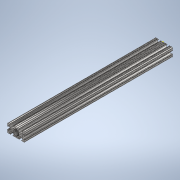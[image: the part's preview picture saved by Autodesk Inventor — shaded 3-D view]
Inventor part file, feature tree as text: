
AUTODESK INVENTOR PART (.ipt)
format: ipt  version: 2020 (Build 240168000, 168)  size: 347,648 bytes
history: native  units: in
note: dims shown in document units (in); Inventor stores cm internally (conversion verified against a paired STEP export)
features: sketch x2, extrude x1
ambient origin geometry x8: Origin, YZ Plane, XZ Plane, XY Plane, X Axis, Y Axis, Z Axis, Center Point
bodies: Solid1 (feature_tree)
feature tree (3):
  extrude  "Extrusion1"  [1 undecoded]
  sketch  "Sketch2"
  sketch  "Sketch1"  dims[d0=17.0in d1=0.0in]
note: 1 required parameter value undecoded (feature->parameter linkage not recoverable at this tier; creation-order binding heuristic only, values carry confidence <= 0.55)
